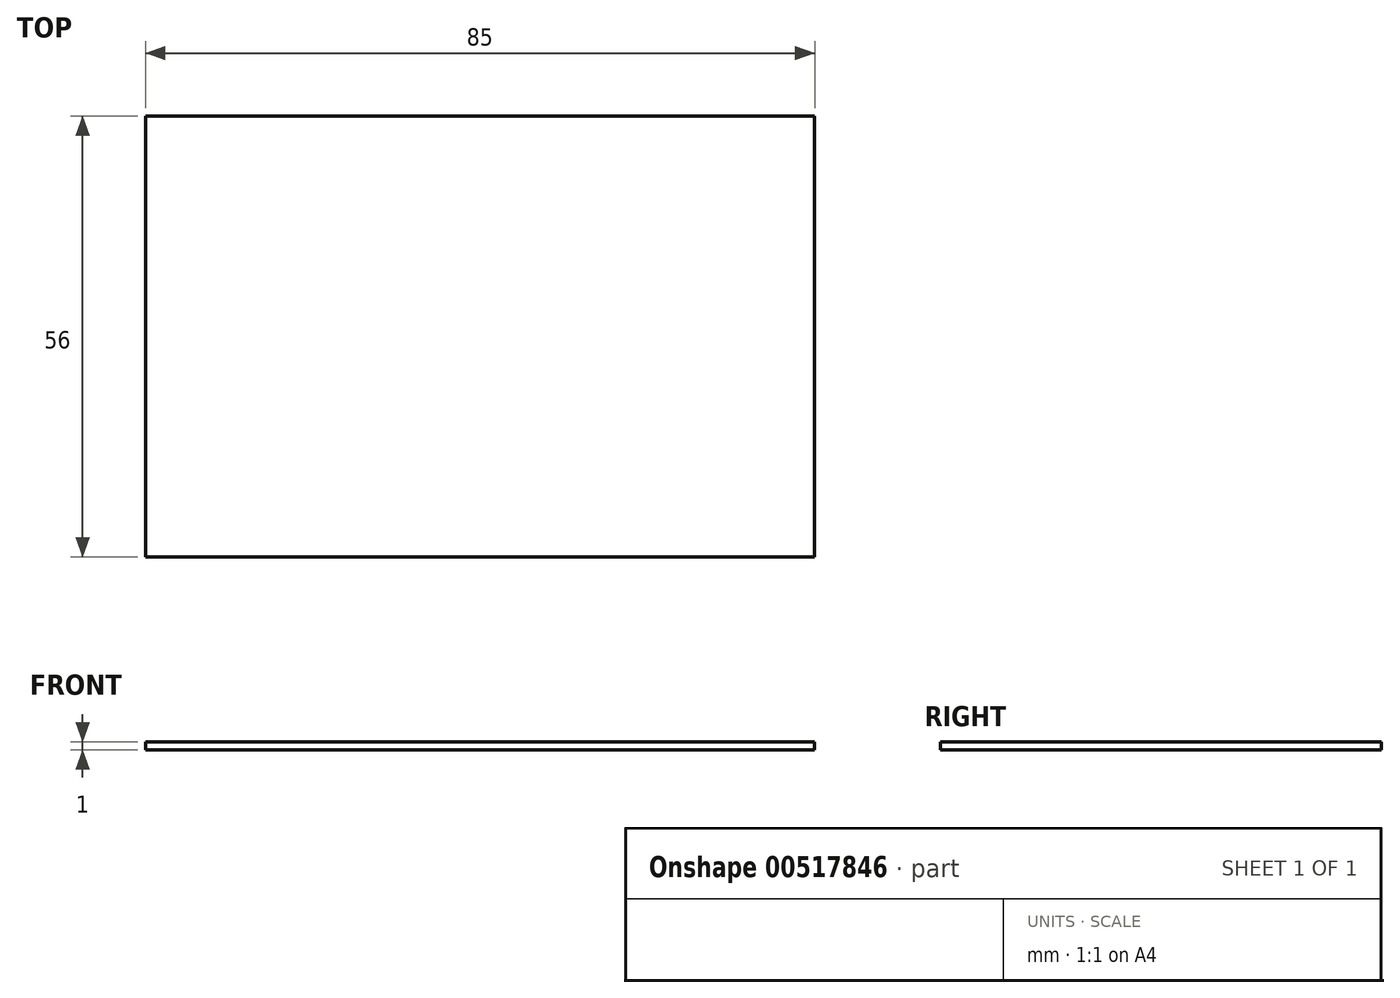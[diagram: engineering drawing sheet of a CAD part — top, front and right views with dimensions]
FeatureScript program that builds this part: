
annotation { "Feature Type Name" : "Feature", "Feature Type Description" : "" }
export const myFeature = defineFeature(function(context is Context, id is Id, definition is map)
    precondition{}
    {
        {
            var Q0;
            Q0=qCreatedBy(makeId("Top.planeOp"),FACE);
            var sketch = newSketch(context, id + "F0", { "sketchPlane" : qUnion([Q0])});
            skLineSegment(sketch, "E0.bottom", {"start": v(-41.6, 20.64) * mm, "end": v(43.4, 20.64) * mm});
            skLineSegment(sketch, "E0.top", {"start": v(-41.6, -35.36) * mm, "end": v(43.4, -35.36) * mm});
            skLineSegment(sketch, "E0.left", {"start": v(-41.6, 20.64) * mm, "end": v(-41.6, -35.36) * mm});
            skLineSegment(sketch, "E0.right", {"start": v(43.4, 20.64) * mm, "end": v(43.4, -35.36) * mm});
            skSolve(sketch);
        }
        {
            var Q0;
            Q0 = qSketchRegion(id + "F0", true);
            extrude(context, id + "F1", {"entities" : qUnion([Q0]), "depth" : 1 * mm, "offsetDistance" : 25 * mm});
        }
    });
